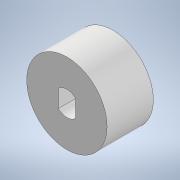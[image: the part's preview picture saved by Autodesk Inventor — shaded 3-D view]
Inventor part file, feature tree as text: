
AUTODESK INVENTOR PART (.ipt)
format: ipt  version: 2022.3 (Build 263350000, 350)  size: 152,064 bytes
history: native  units: mm
features: reference x3, other x3, extrude x2, sketch x2, projected_geometry x1
ambient origin geometry x8: Origin, YZ Plane, XZ Plane, XY Plane, X Axis, Y Axis, Z Axis, Center Point
bodies: Solid1 (feature_tree)
feature tree (11):
  extrude  "Extrusion1"  Depth=10.0mm TaperAngle=0.0deg
  extrude  "Extrusion2"  TaperAngle=0.0deg  [1 undecoded]
  sketch  "Sketch1"  dims[d0=1.0mm d1=10.0mm d2=0.0mm]
  reference  "Reference1"
  reference  "Reference2"
  reference  "Reference3"
  sketch  "Sketch2"  dims[d3=0.5mm d4=0.0mm d5=0.0mm]
  projected_geometry  "Projected Loop1"
  other  "<userpath>\Documents\Inventor\NanoSumo\Przekładnia.iam"
  other  "Przekładnia.iam"
  other  "Moteur - Engrenage 1:1"
note: 1 required parameter value undecoded (feature->parameter linkage not recoverable at this tier; creation-order binding heuristic only, values carry confidence <= 0.55)
